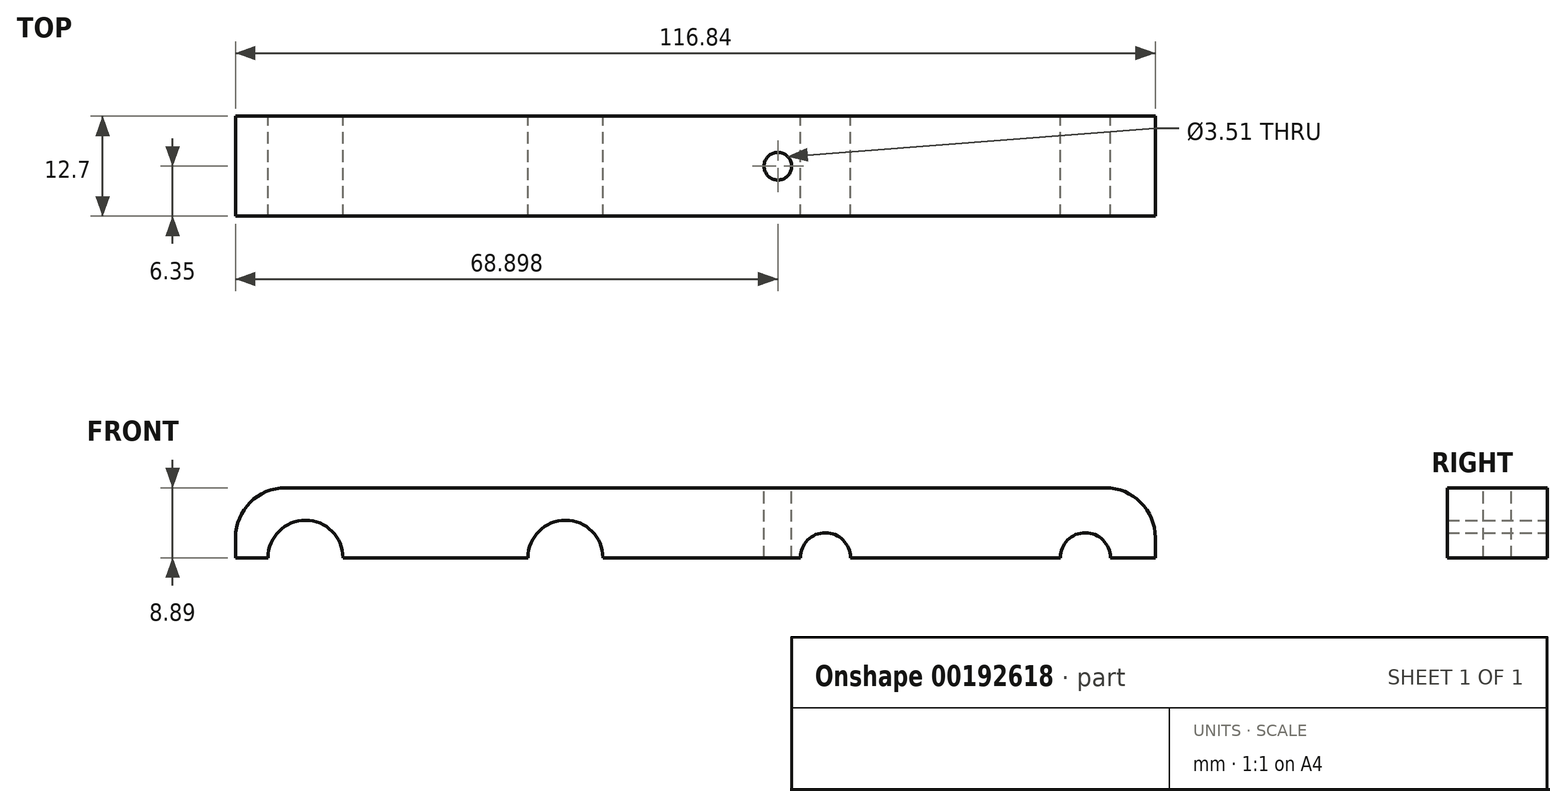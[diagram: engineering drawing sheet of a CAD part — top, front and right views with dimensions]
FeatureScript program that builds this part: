
annotation { "Feature Type Name" : "Feature", "Feature Type Description" : "" }
export const myFeature = defineFeature(function(context is Context, id is Id, definition is map)
    precondition{}
    {
        {
            var Q0;
            Q0=qCreatedBy(makeId("Front.planeOp"),FACE);
            var sketch = newSketch(context, id + "F0", { "sketchPlane" : qUnion([Q0])});
            skArc(sketch, "E0", {"start": v(4.76, 0) * mm, "mid": v(0, 4.76) * mm, "end": v(-4.76, 0) * mm});
            skArc(sketch, "E1", {"start": v(37.78, 0) * mm, "mid": v(33.02, 4.76) * mm, "end": v(28.26, 0) * mm});
            skArc(sketch, "E2", {"start": v(69.22, 0) * mm, "mid": v(66.04, 3.18) * mm, "end": v(62.87, 0) * mm});
            skArc(sketch, "E3", {"start": v(102.23, 0) * mm, "mid": v(99.06, 3.18) * mm, "end": v(95.89, 0) * mm});
            skLineSegment(sketch, "E4.bottom", {"start": v(-8.9, 0) * mm, "end": v(-4.76, 0) * mm});
            skLineSegment(sketch, "E4.top", {"start": v(-2.54, 8.9) * mm, "end": v(101.6, 8.9) * mm});
            skLineSegment(sketch, "E4.left", {"start": v(-8.9, 0) * mm, "end": v(-8.9, 2.54) * mm});
            skLineSegment(sketch, "E4.right", {"start": v(107.95, 0) * mm, "end": v(107.95, 2.54) * mm});
            skLineSegment(sketch, "E5.trimOffspring", {"start": v(4.76, 0) * mm, "end": v(28.26, 0) * mm});
            skLineSegment(sketch, "E6.trimOffspring", {"start": v(37.78, 0) * mm, "end": v(62.87, 0) * mm});
            skLineSegment(sketch, "E7.trimOffspring", {"start": v(69.22, 0) * mm, "end": v(95.89, 0) * mm});
            skLineSegment(sketch, "E8.trimOffspring", {"start": v(102.23, 0) * mm, "end": v(107.95, 0) * mm});
            skPoint(sketch, "E9.visualSharp", {"position": v(-8.9, 8.9) * mm});
            skArc(sketch, "E9.filletArc", {"start": v(-2.54, 8.9) * mm, "mid": v(-7.03, 7.03) * mm, "end": v(-8.9, 2.54) * mm});
            skPoint(sketch, "E10.visualSharp", {"position": v(107.95, 8.9) * mm});
            skArc(sketch, "E10.filletArc", {"start": v(107.95, 2.54) * mm, "mid": v(106.1, 7.03) * mm, "end": v(101.6, 8.9) * mm});
            skLineSegment(sketch, "E11", {"start": v(57.15, 0) * mm, "end": v(57.15, 8.9) * mm, "construction": true});
            skSolve(sketch);
        }
        {
            var Q0;
            Q0 = qSketchRegion(id + "F0", true);
            extrude(context, id + "F1", {"entities" : qUnion([Q0]), "depth" : 12.7 * mm});
        }
        {
            var Q0;
            Q0=makeQuery(id+"F1.opExtrude","SWEPT_FACE",FACE,{"disambiguationData":[OSD([sQuery(id+"F0.wireOp",EDGE,"E4.top")])]});
            var sketch = newSketch(context, id + "F2", { "sketchPlane" : qUnion([Q0])});
            skCircle(sketch, "E12", {"center": v(60, -6.35) * mm, "radius": 1.75 * mm});
            skSolve(sketch);
        }
        {
            var Q0;
            Q0 = qSketchRegion(id + "F2", true);
            extrude(context, id + "F3", {"entities" : qUnion([Q0]), "operationType" : NewBodyOperationType.REMOVE, "oppositeDirection" : true, "depth" : 25.4 * mm});
        }
    });
